# Revit family: BLOX
name_source: partatom
category: Lighting Fixtures
units: mm (PartAtom-declared; Revit-internal decimal feet)

## family parameters
Cut with Voids When Loaded = No
Host = Face
Light Source = Yes
OmniClass Number = 23.80.70.11
OmniClass Title = Luminaries for Internal Lighting
Part Type = Normal
Room Calculation Point = No
Round Connector Dimension = Use Diameter
Shared = No

## types (3) — shared parameters
Apparent Load = 3 VA
Color Filter = 16777215
Default Elevation = 48 "
Dimming Lamp Color Temperature Shift = <None>
Emit Shape Visible in Rendering = No
Emit from Rectangle Length = 4 "
Emit from Rectangle Width = 4 "
Housing Material = Standard
Illuminated Surface Material = Light
Light Box Length = 23.75 "
Light Box Width = 23.75 "
Manufacturer = ARON LIGHTING®
Model = BLOX
Number Of Pole = 1
Tilt Angle = 90.00°
URL = https://www.aronlighting.com
Voltage = 120 V
zero-valued in all types: Cost

## per-type parameters (varying)
| type | Photometric Web File |
| PL18806-001A 4INCH FLD Flush AID FnRpt.ies | PL18806-001A 4INCH FLD Flush AID FnRpt.ies |
| PL18804-001A 2in FLD Regressed AID FnRpt | PL18804-001A 2in FLD Regressed AID FnRpt.ies |
| PL18805-001A 4in FLD Regressed AID FnRpt | PL18805-001A 4in FLD Regressed AID FnRpt.ies |

## geometry (parser evidence)
native form markers: Sweep x2
no freeform markers — native parametric forms only
